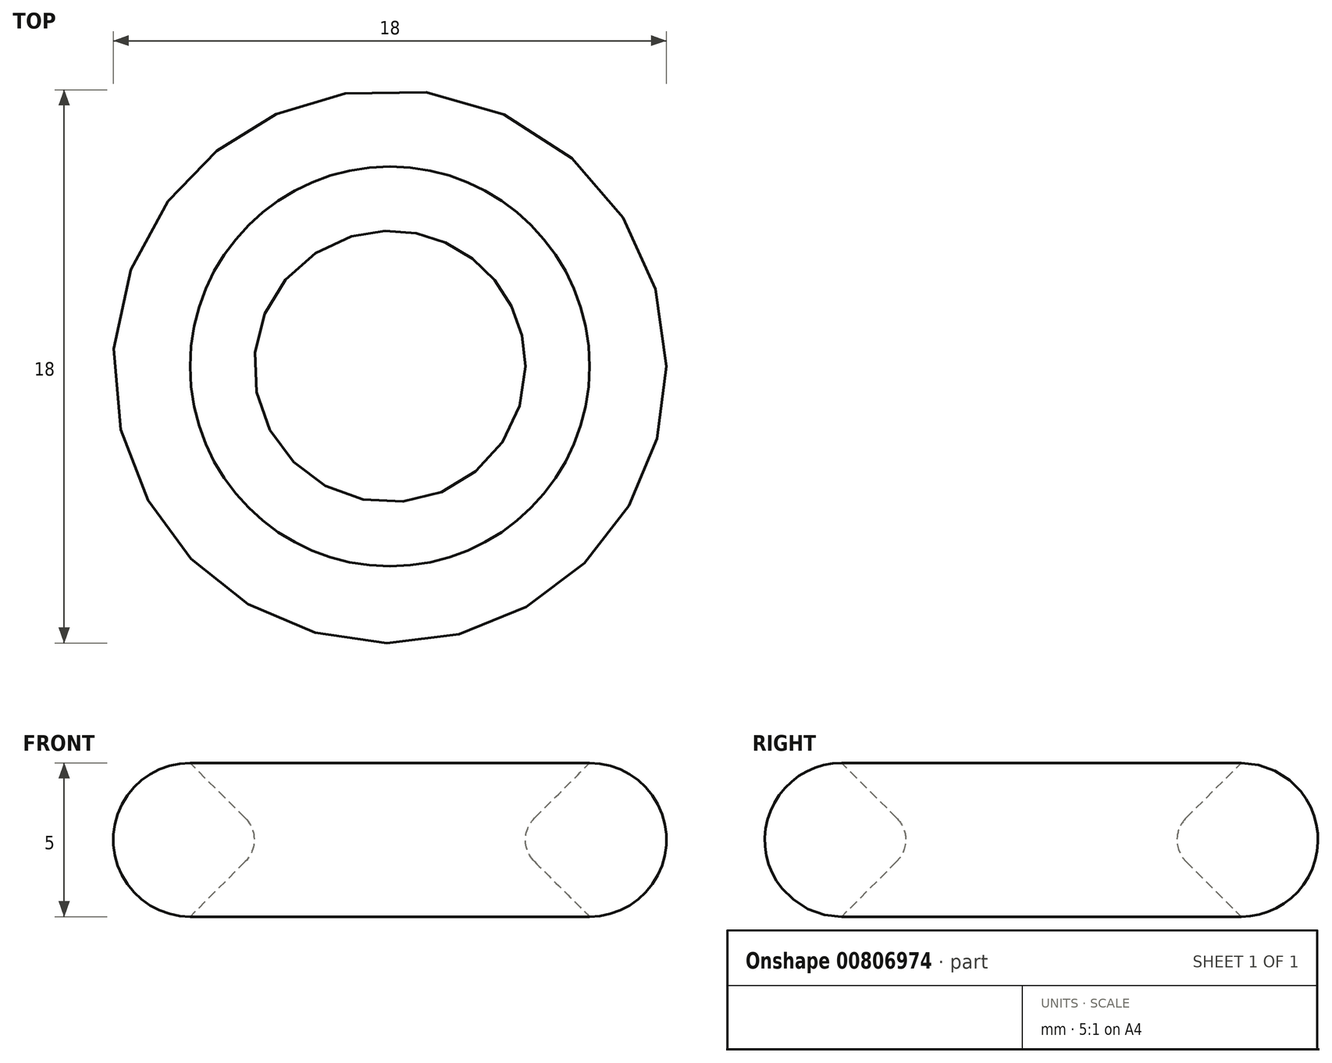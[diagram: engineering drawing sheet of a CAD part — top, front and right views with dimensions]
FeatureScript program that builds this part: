
annotation { "Feature Type Name" : "Feature", "Feature Type Description" : "" }
export const myFeature = defineFeature(function(context is Context, id is Id, definition is map)
    precondition{}
    {
        {
            var Q0;
            Q0=qCreatedBy(makeId("Top.planeOp"),FACE);
            var sketch = newSketch(context, id + "F0", { "sketchPlane" : qUnion([Q0])});
            skCircle(sketch, "E0", {"center": v(0, 0) * mm, "radius": 4 * mm});
            skCircle(sketch, "E1", {"center": v(0, 0) * mm, "radius": 9 * mm});
            skSolve(sketch);
        }
        {
            var Q0;
            Q0 = qSketchRegion(id + "F0", true);
            var Q1;
            Q1=makeQuery(id+"F0.imprint","IMPRINT",FACE,{"disambiguationData":[TD([[makeQuery(id+"F0.imprint","IMPRINT",EDGE,{"derivedFrom":sQuery(id+"F0.wireOp",EDGE,"E0")}),-1.0]])]});
            extrude(context, id + "F1", {"entities" : qUnion([Q0, Q1]), "depth" : 5 * mm, "offsetDistance" : 25 * mm});
        }
        {
            var Q0;
            Q0=makeQuery(id+"F1.opExtrude","CAP_EDGE",EDGE,{"disambiguationData":[OSD([sQuery(id+"F0.wireOp",EDGE,"E1")])],"isStart":false});
            var Q1;
            Q1=makeQuery(id+"F1.opExtrude","CAP_EDGE",EDGE,{"disambiguationData":[OSD([sQuery(id+"F0.wireOp",EDGE,"E1")])],"isStart":true});
            fillet(context, id + "F2", {"entities" : qUnion([Q0, Q1]), "radius" : 2.5 * mm, "tangentPropagation" : true, "allowEdgeOverflow" : false});
        }
        {
            var Q0;
            Q0=makeQuery(id+"F1.opExtrude","SWEPT_FACE",FACE,{"disambiguationData":[OSD([sQuery(id+"F0.wireOp",EDGE,"E0")])]});
            chamfer(context, id + "F3", {"entities" : qUnion([Q0]), "width" : 2.5 * mm, "tangentPropagation" : true});
        }
        {
            var Q0;
            {var subQ0=sQuery(id+"F0.wireOp",EDGE,"E0");Q0=makeQuery(id+"F3.opChamfer","BLEND_EDGE",EDGE,{"blendedFrom":[makeQuery(id+"F1.opExtrude","CAP_EDGE",EDGE,{"disambiguationData":[OSD([subQ0])],"isStart":true}),makeQuery(id+"F1.opExtrude","CAP_EDGE",EDGE,{"disambiguationData":[OSD([subQ0])],"isStart":false})],"blendedInto":[]});}
            fillet(context, id + "F4", {"entities" : qUnion([Q0]), "radius" : 1 * mm, "tangentPropagation" : true, "allowEdgeOverflow" : false});
        }
    });
